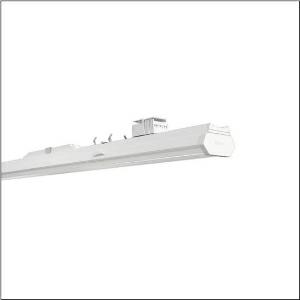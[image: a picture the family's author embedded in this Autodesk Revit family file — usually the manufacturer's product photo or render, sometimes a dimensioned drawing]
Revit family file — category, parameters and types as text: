
# Revit family: licross_r__21_protected_mo_52tp11dn48xg_4e19
name_source: partatom
category: Lighting Fixtures
units: mm (PartAtom-declared; Revit-internal decimal feet)

## family parameters
Cut with Voids When Loaded = No
Host = Face
Light Source = No
Part Type = Normal
Room Calculation Point = No
Round Connector Dimension = Use Diameter
Shared = No

## types (1)
- --- (1 x LED, 8000 lm, 45.5 W, 4000K)
    Apparent Load = 46 VA
    CIE Flux Codes = 83 94 98 100 100
    Color Rendering = 80
    Color Temperature = 4000K
    Default Elevation = 1800 mm
    Description = Licross® 21 Protected MO, luminaire insert, of sheet steel, galvanised, coil coated, white, length: 1.500mm, width: 90mm, height: 103mm, LED rated luminous flux: 8.000lm, light colour: 840, control gear: DALI 2, with plug, 5-pole, with phase selection, mains connection: 220..240V, AC, 50/60Hz, rated input power: 46W, halogen-free wiring, primary light control with lens, of plastic, primary optical cover: cover, of PMMA, light emission: direct distribution, primary light characteristic: symmetric, protection rating (complete): IP64, insulation class (complete): insulation class I (protective earthing), certification: CE, ENEC, VDE, UKCA, protection symbol: D if used in an environment with conductive dust loads with corresponding accessories, impact resistance: IK06, permissible ambient temperature for indoor applications: -25..+45°C, corresponds to IFS (International Featured Standards) requirements for safety and quality in the food industry, reducing of maximum allowable ambient temperature of 5°C with ceiling mounting, LABS conformity tested according to VDMA 24364:2018-05, packaging unit: 1 piece
    Height = 92 mm
    Lamp = 1 x LED
    Lamp Light Flux = 8000 lm
    Lamp Power = 45.5 W
    Lamp count = 1
    Length = 1500 mm
    Luminous efficacy = 176 lm/W
    Manufacturer = Siteco
    ModVariant = No
    Model = 52TP11DN48XG
    Mounting Place = Ceiling
    Mounting Type = Pendant
    Number of Poles = 1
    OnlyDefault = Yes
    Power Factor = 1
    Product Name = Licross® 21 Protected MO
    Product group = luminaire insert
    ProductGroupID = 902
    Protection Class = Protection class I
    Protection Degree = IP 64
    RLX_Detail_Level = 1
    RLX_Emergency_Light_Flux = 0 lm
    RLX_Emergency_Type = 0
    RLX_Emergency_Type_DB = No
    RlxData = <blob elided: 24117 chars, md5=8e1c28be>
    Socket = socket
    Standby Power = 0 W
    System Light Flux = 8000 lm
    System Power = 46 W
    Type Comments = factory setting: luminous flux: 100 % | dim-lin: 254 | 307 mA
    Type Image = l_1256148.jpg
    URL = http://relux.com
    VarID = @adj_128174
    Voltage = 0 V
    Weight = 0.00 kg
    Width = 88 mm

## geometry (parser evidence)
native form markers: Blend x4, Sweep x13
no freeform markers — native parametric forms only
